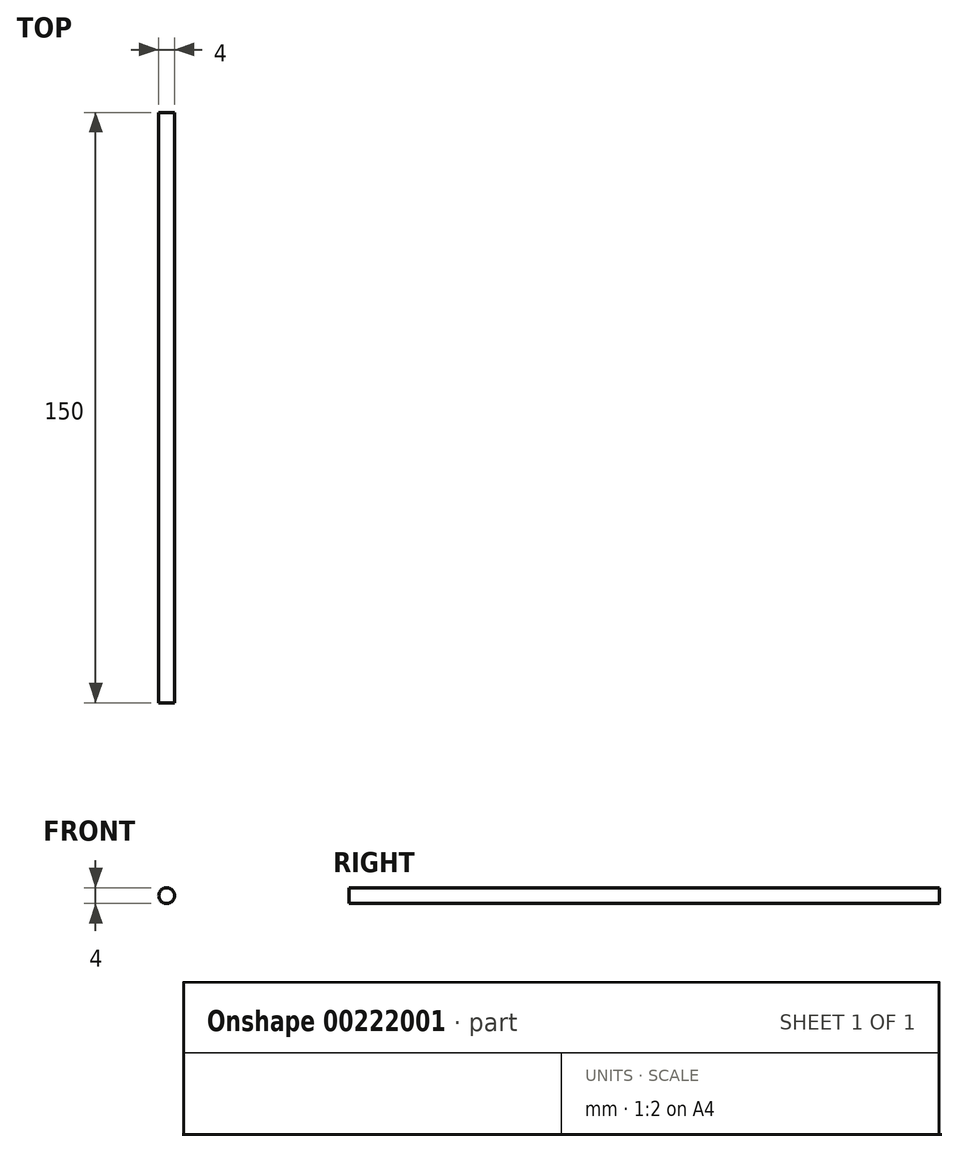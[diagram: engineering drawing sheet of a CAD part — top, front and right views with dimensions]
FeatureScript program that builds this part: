
annotation { "Feature Type Name" : "Feature", "Feature Type Description" : "" }
export const myFeature = defineFeature(function(context is Context, id is Id, definition is map)
    precondition{}
    {
        {
            var Q0;
            Q0=qCreatedBy(makeId("Front.planeOp"),FACE);
            var sketch = newSketch(context, id + "F0", { "sketchPlane" : qUnion([Q0])});
            skCircle(sketch, "E0", {"center": v(0, 0) * mm, "radius": 2 * mm});
            skSolve(sketch);
        }
        {
            var Q0;
            Q0=makeQuery(id+"F0.imprint","IMPRINT",FACE,{"disambiguationData":[TD([[makeQuery(id+"F0.imprint","IMPRINT",EDGE,{"derivedFrom":sQuery(id+"F0.wireOp",EDGE,"E0")}),1.0]])]});
            extrude(context, id + "F1", {"entities" : qUnion([Q0]), "depth" : 150 * mm, "offsetDistance" : 25.4 * mm});
        }
    });
